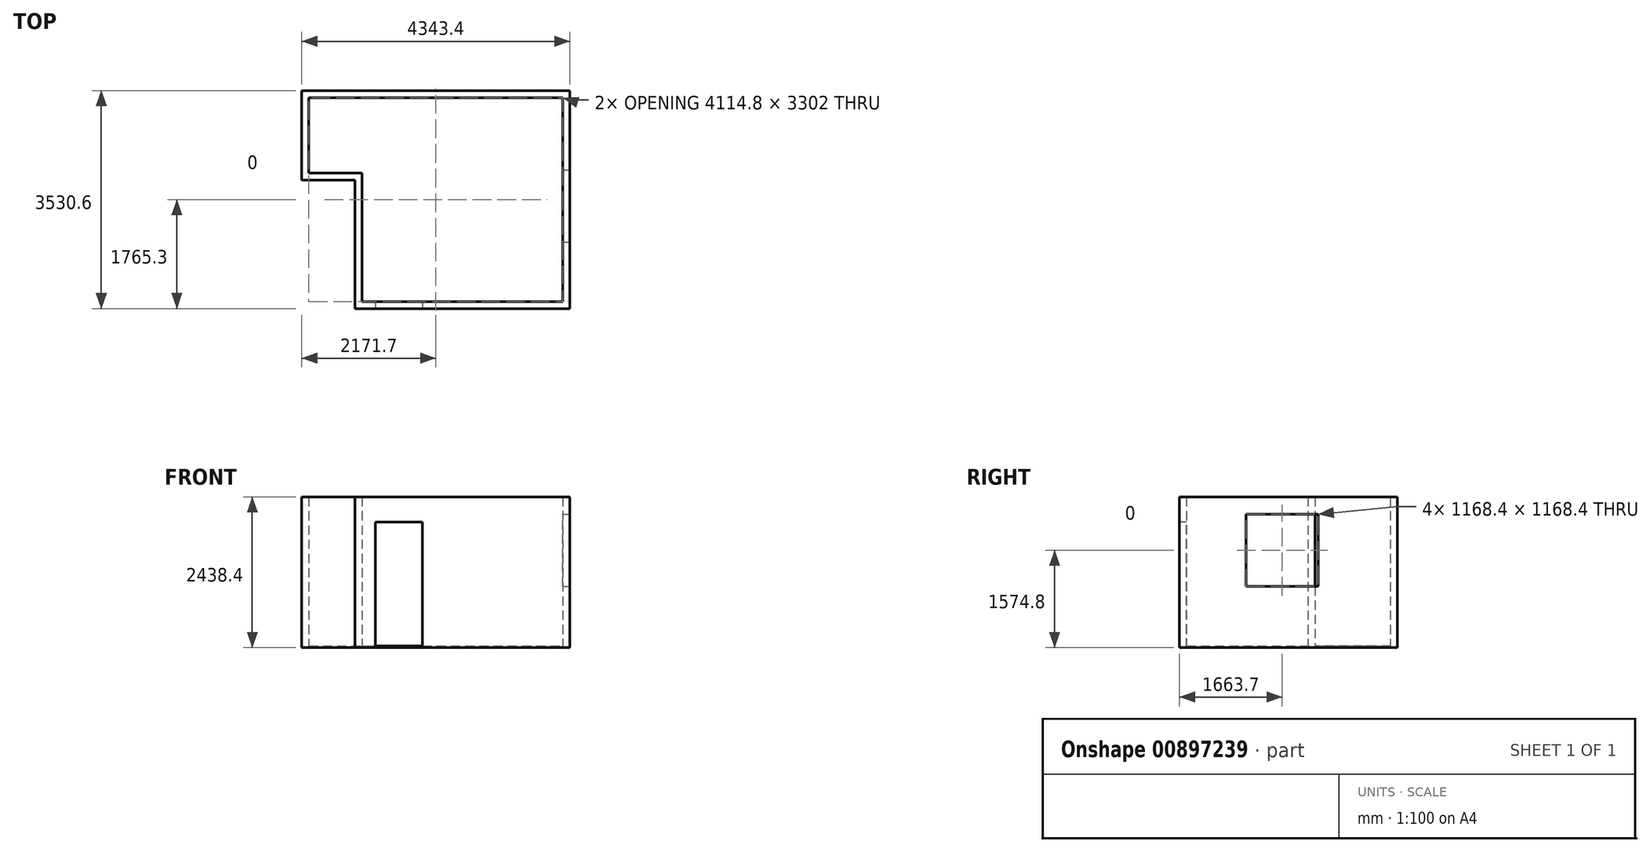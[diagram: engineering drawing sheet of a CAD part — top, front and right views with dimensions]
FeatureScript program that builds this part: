
annotation { "Feature Type Name" : "Feature", "Feature Type Description" : "" }
export const myFeature = defineFeature(function(context is Context, id is Id, definition is map)
    precondition{}
    {
        {
            var Q0;
            Q0=qCreatedBy(makeId("Top.planeOp"),FACE);
            var sketch = newSketch(context, id + "F0", { "sketchPlane" : qUnion([Q0])});
            skLineSegment(sketch, "E0.bottom", {"start": v(-1625.6, -1651) * mm, "end": v(1625.6, -1651) * mm});
            skLineSegment(sketch, "E0.top", {"start": v(-1625.6, 1651) * mm, "end": v(1625.6, 1651) * mm});
            skLineSegment(sketch, "E0.left", {"start": v(-1625.6, -1651) * mm, "end": v(-1625.6, 1651) * mm});
            skLineSegment(sketch, "E0.right", {"start": v(1625.6, -1651) * mm, "end": v(1625.6, 1651) * mm});
            skPoint(sketch, "E0.middle", {"position": v(0, 0) * mm});
            skLineSegment(sketch, "E1", {"start": v(-1625.6, 1651) * mm, "end": v(-2489.2, 1651) * mm});
            skLineSegment(sketch, "E2", {"start": v(-2489.2, 1651) * mm, "end": v(-2489.2, 431.8) * mm});
            skLineSegment(sketch, "E3", {"start": v(-2489.2, 431.8) * mm, "end": v(-1625.6, 431.8) * mm});
            skSolve(sketch);
        }
        {
            var Q0;
            Q0 = qSketchRegion(id + "F0", true);
            extrude(context, id + "F1", {"entities" : qUnion([Q0]), "depth" : 25.4 * mm, "offsetDistance" : 25.4 * mm});
        }
        {
            var Q0;
            Q0=qCreatedBy(makeId("Top.planeOp"),FACE);
            var sketch = newSketch(context, id + "F2", { "sketchPlane" : qUnion([Q0])});
            skLineSegment(sketch, "E4.0", {"start": v(-2489.2, 1651) * mm, "end": v(-2489.2, 431.8) * mm});
            skLineSegment(sketch, "E5.0", {"start": v(-2489.2, 1651) * mm, "end": v(1625.6, 1651) * mm});
            skLineSegment(sketch, "E6.0", {"start": v(-2489.2, 431.8) * mm, "end": v(-1625.6, 431.8) * mm});
            skLineSegment(sketch, "E7.0", {"start": v(-1625.6, -1651) * mm, "end": v(-1625.6, 431.8) * mm});
            skLineSegment(sketch, "E8.0", {"start": v(-1625.6, -1651) * mm, "end": v(1625.6, -1651) * mm});
            skLineSegment(sketch, "E9.0", {"start": v(1625.6, -1651) * mm, "end": v(1625.6, 1651) * mm});
            skLineSegment(sketch, "E10.0", {"start": v(-2603.5, 1765.3) * mm, "end": v(-2603.5, 317.5) * mm});
            skLineSegment(sketch, "E10.1", {"start": v(1739.9, -1765.3) * mm, "end": v(1739.9, 1765.3) * mm});
            skLineSegment(sketch, "E10.2", {"start": v(-1739.9, -1765.3) * mm, "end": v(1739.9, -1765.3) * mm});
            skLineSegment(sketch, "E10.3", {"start": v(-2603.5, 1765.3) * mm, "end": v(1739.9, 1765.3) * mm});
            skLineSegment(sketch, "E10.4", {"start": v(-1739.9, -1765.3) * mm, "end": v(-1739.9, 317.5) * mm});
            skLineSegment(sketch, "E10.5", {"start": v(-2603.5, 317.5) * mm, "end": v(-1739.9, 317.5) * mm});
            skSolve(sketch);
        }
        {
            var Q0;
            Q0 = qSketchRegion(id + "F2", true);
            extrude(context, id + "F3", {"entities" : qUnion([Q0]), "depth" : 2438.4 * mm, "offsetDistance" : 25.4 * mm});
        }
        {
            var Q0;
            Q0=makeQuery(id+"F3.opExtrude","SWEPT_FACE",FACE,{"disambiguationData":[OSD([sQuery(id+"F2.wireOp",EDGE,"E10.2")])]});
            var sketch = newSketch(context, id + "F4", { "sketchPlane" : qUnion([Q0])});
            skLineSegment(sketch, "E11.bottom", {"start": v(-1409.7, 0) * mm, "end": v(-647.7, 0) * mm});
            skLineSegment(sketch, "E11.top", {"start": v(-1409.7, 2032) * mm, "end": v(-647.7, 2032) * mm});
            skLineSegment(sketch, "E11.left", {"start": v(-1409.7, 0) * mm, "end": v(-1409.7, 2032) * mm});
            skLineSegment(sketch, "E11.right", {"start": v(-647.7, 0) * mm, "end": v(-647.7, 2032) * mm});
            skSolve(sketch);
        }
        {
            var Q0;
            Q0 = qSketchRegion(id + "F4", true);
            var Q1;
            Q1=makeQuery(id+"F3.opExtrude","SWEPT_FACE",FACE,{"disambiguationData":[OSD([sQuery(id+"F2.wireOp",EDGE,"E8.0")])]});
            extrude(context, id + "F5", {"entities" : qUnion([Q0]), "operationType" : NewBodyOperationType.REMOVE, "endBound" : BoundingType.UP_TO_SURFACE, "oppositeDirection" : true, "depth" : 25.4 * mm, "endBoundEntityFace" : qUnion([Q1]), "offsetDistance" : 25.4 * mm});
        }
        {
            var Q0;
            Q0=makeQuery(id+"F3.opExtrude","SWEPT_FACE",FACE,{"disambiguationData":[OSD([sQuery(id+"F2.wireOp",EDGE,"E10.1")])]});
            var sketch = newSketch(context, id + "F6", { "sketchPlane" : qUnion([Q0])});
            skLineSegment(sketch, "E12.bottom", {"start": v(-685.8, 990.6) * mm, "end": v(482.6, 990.6) * mm});
            skLineSegment(sketch, "E12.top", {"start": v(-685.8, 2159) * mm, "end": v(482.6, 2159) * mm});
            skLineSegment(sketch, "E12.left", {"start": v(-685.8, 990.6) * mm, "end": v(-685.8, 2159) * mm});
            skLineSegment(sketch, "E12.right", {"start": v(482.6, 990.6) * mm, "end": v(482.6, 2159) * mm});
            skSolve(sketch);
        }
        {
            var Q0;
            Q0 = qSketchRegion(id + "F6", true);
            var Q1;
            Q1=makeQuery(id+"F3.opExtrude","SWEPT_FACE",FACE,{"disambiguationData":[OSD([sQuery(id+"F2.wireOp",EDGE,"E9.0")])]});
            extrude(context, id + "F7", {"entities" : qUnion([Q0]), "operationType" : NewBodyOperationType.REMOVE, "endBound" : BoundingType.UP_TO_SURFACE, "oppositeDirection" : true, "depth" : 25.4 * mm, "endBoundEntityFace" : qUnion([Q1]), "offsetDistance" : 25.4 * mm});
        }
    });
